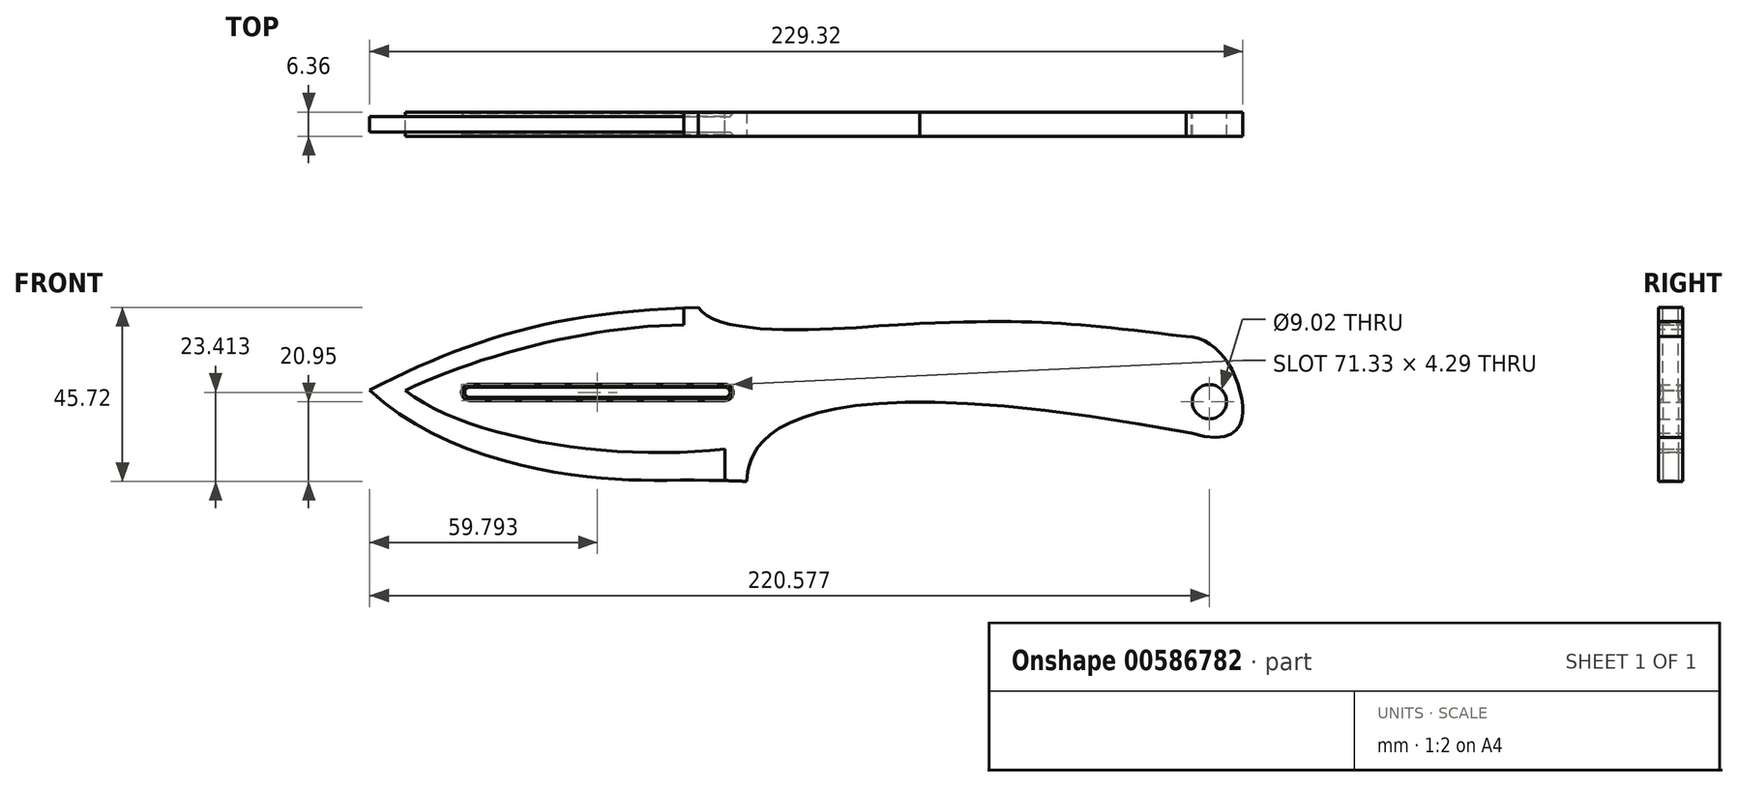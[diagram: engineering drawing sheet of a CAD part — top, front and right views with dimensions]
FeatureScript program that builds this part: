
annotation { "Feature Type Name" : "Feature", "Feature Type Description" : "" }
export const myFeature = defineFeature(function(context is Context, id is Id, definition is map)
    precondition{}
    {
        {
            var Q0;
            Q0=qCreatedBy(makeId("Front.planeOp"),FACE);
            var sketch = newSketch(context, id + "F0", { "sketchPlane" : qUnion([Q0])});
            skFitSpline(sketch, "E0", {"points": [v(-99.06, 15.47) * mm, v(0, 37.23) * mm], "startDerivative": vector(85.45, 43.45) * mm, "endDerivative": vector(137.12, -1.65) * mm});
            skFitSpline(sketch, "E1", {"points": [v(-99.06, 15.47) * mm, v(-40.1, -7.53) * mm, v(0, -8.57) * mm], "startDerivative": vector(87.41, -83.36) * mm, "endDerivative": vector(117.89, -5.53) * mm});
            skFitSpline(sketch, "E2", {"points": [v(0, -8.57) * mm, v(116.84, 4.12) * mm], "startDerivative": vector(0.75, 25.7) * mm, "endDerivative": vector(335.55, -63.02) * mm});
            skFitSpline(sketch, "E3", {"points": [v(-12.7, 37.15) * mm, v(45.44, 32.92) * mm], "startDerivative": vector(17.5, -29) * mm, "endDerivative": vector(32.9, 0.77) * mm});
            skFitSpline(sketch, "E4", {"points": [v(45.44, 32.92) * mm, v(115.35, 29.52) * mm], "startDerivative": vector(96.73, 3.81) * mm, "endDerivative": vector(88.73, -10.48) * mm});
            skFitSpline(sketch, "E5", {"points": [v(115.35, 29.52) * mm, v(129.54, 15.2) * mm, v(116.84, 4.12) * mm], "startDerivative": vector(40.27, -0.16) * mm, "endDerivative": vector(-86.24, 25.9) * mm});
            skFitSpline(sketch, "E6", {"points": [v(-89.68, 15.35) * mm, v(-5.75, 0) * mm], "startDerivative": vector(49.83, -38.63) * mm, "endDerivative": vector(88.15, 10.48) * mm});
            skFitSpline(sketch, "E7", {"points": [v(-89.68, 15.35) * mm, v(-16.55, 32.54) * mm], "startDerivative": vector(57.5, 27.79) * mm, "endDerivative": vector(70.9, 0) * mm});
            skLineSegment(sketch, "E8", {"start": v(-16.55, 32.54) * mm, "end": v(-16.55, 37.03) * mm});
            skLineSegment(sketch, "E9", {"start": v(-5.75, 0) * mm, "end": v(-5.75, -8.35) * mm});
            skLineSegment(sketch, "E10", {"start": v(-99.06, 15.47) * mm, "end": v(-89.68, 15.35) * mm});
            skLineSegment(sketch, "E11", {"start": v(-16.55, 37.03) * mm, "end": v(-12.7, 37.15) * mm});
            skLineSegment(sketch, "E12", {"start": v(-5.75, -8.35) * mm, "end": v(0, -8.57) * mm});
            skLineSegment(sketch, "E13", {"start": v(116.84, 4.12) * mm, "end": v(116.84, 4.12) * mm});
            skCircle(sketch, "E14", {"center": v(121.52, 12.38) * mm, "radius": 4.5 * mm});
            skLineSegment(sketch, "E15", {"start": v(-72.79, 16.99) * mm, "end": v(-5.75, 16.99) * mm});
            skLineSegment(sketch, "E16", {"start": v(-72.79, 12.7) * mm, "end": v(-5.75, 12.7) * mm});
            skArc(sketch, "E17", {"start": v(-72.79, 16.99) * mm, "mid": v(-74.93, 14.84) * mm, "end": v(-72.79, 12.7) * mm});
            skArc(sketch, "E18", {"start": v(-5.75, 12.7) * mm, "mid": v(-3.6, 14.84) * mm, "end": v(-5.75, 16.99) * mm});
            skSolve(sketch);
        }
        {
            var Q0;
            {var subQ2=sQuery(id+"F0.wireOp",EDGE,"E2");Q0=makeQuery(id+"F0.imprint","IMPRINT",FACE,{"disambiguationData":[TD([[makeQuery(id+"F0.imprint","IMPRINT",EDGE,{"derivedFrom":subQ2}),1.0]])]});}
            extrude(context, id + "F1", {"entities" : qUnion([Q0]), "endBound" : BoundingType.SYMMETRIC, "depth" : 6.35 * mm, "offsetDistance" : 25.4 * mm});
        }
        {
            var Q0;
            Q0=makeQuery(id+"F0.imprint","IMPRINT",FACE,{"disambiguationData":[TD([[makeQuery(id+"F0.imprint","IMPRINT",EDGE,{"derivedFrom":sQuery(id+"F0.wireOp",EDGE,"E15")}),-1.0]])]});
            extrude(context, id + "F2", {"entities" : qUnion([Q0]), "operationType" : NewBodyOperationType.ADD, "endBound" : BoundingType.SYMMETRIC, "depth" : 4.06 * mm, "offsetDistance" : 25.4 * mm});
        }
        {
            var Q0;
            Q0=makeQuery(id+"F2.opExtrude","CAP_FACE",FACE,{"disambiguationData":[OSD([sQuery(id+"F0.wireOp",EDGE,"E15"),sQuery(id+"F0.wireOp",EDGE,"E16"),sQuery(id+"F0.wireOp",EDGE,"E17"),sQuery(id+"F0.wireOp",EDGE,"E18")])],"isStart":true});
            var Q1;
            Q1=makeQuery(id+"F2.opExtrude","CAP_FACE",FACE,{"disambiguationData":[OSD([sQuery(id+"F0.wireOp",EDGE,"E15"),sQuery(id+"F0.wireOp",EDGE,"E16"),sQuery(id+"F0.wireOp",EDGE,"E17"),sQuery(id+"F0.wireOp",EDGE,"E18")])],"isStart":false});
            chamfer(context, id + "F3", {"entities" : qUnion([Q0, Q1]), "width" : 0.81 * mm, "tangentPropagation" : true});
        }
        {
            var Q0;
            Q0=makeQuery(id+"F0.imprint","IMPRINT",FACE,{"disambiguationData":[TD([[makeQuery(id+"F0.imprint","IMPRINT",EDGE,{"derivedFrom":sQuery(id+"F0.wireOp",EDGE,"E6")}),-1.0]])]});
            var Q1;
            Q1=makeQuery(id+"F0.imprint","IMPRINT",FACE,{"disambiguationData":[TD([[makeQuery(id+"F0.imprint","IMPRINT",EDGE,{"derivedFrom":sQuery(id+"F0.wireOp",EDGE,"E7")}),1.0]])]});
            extrude(context, id + "F4", {"entities" : qUnion([Q0, Q1]), "endBound" : BoundingType.SYMMETRIC, "depth" : 4.06 * mm, "offsetDistance" : 25.4 * mm});
        }
    });
